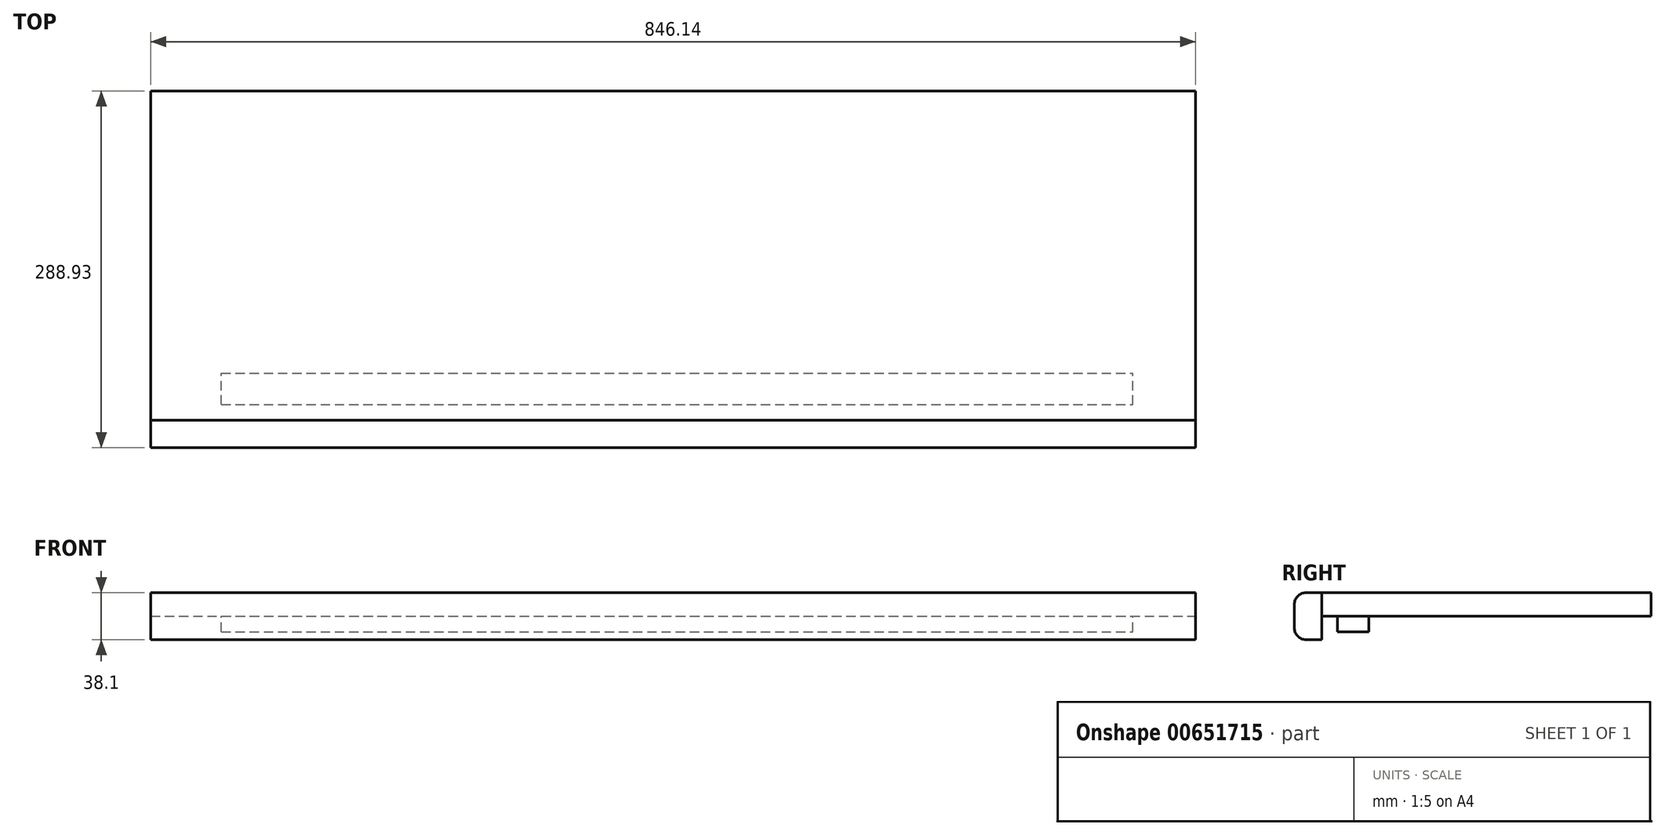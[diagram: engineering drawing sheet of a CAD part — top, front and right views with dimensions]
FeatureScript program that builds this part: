
annotation { "Feature Type Name" : "Feature", "Feature Type Description" : "" }
export const myFeature = defineFeature(function(context is Context, id is Id, definition is map)
    precondition{}
    {
        {
            var Q0;
            Q0=qCreatedBy(makeId("Top.planeOp"),FACE);
            var sketch = newSketch(context, id + "F0", { "sketchPlane" : qUnion([Q0])});
            skLineSegment(sketch, "E0.bottom", {"start": v(0, 0) * mm, "end": v(846.14, 0) * mm});
            skLineSegment(sketch, "E0.top", {"start": v(0, 266.7) * mm, "end": v(846.14, 266.7) * mm});
            skLineSegment(sketch, "E0.left", {"start": v(0, 0) * mm, "end": v(0, 266.7) * mm});
            skLineSegment(sketch, "E0.right", {"start": v(846.14, 0) * mm, "end": v(846.14, 266.7) * mm});
            skSolve(sketch);
        }
        {
            var Q0;
            Q0=makeQuery(id+"F0.imprint","IMPRINT",FACE,{"disambiguationData":[TD([[makeQuery(id+"F0.imprint","IMPRINT",EDGE,{"derivedFrom":sQuery(id+"F0.wireOp",EDGE,"E0.bottom")}),1.0]])]});
            extrude(context, id + "F1", {"entities" : qUnion([Q0]), "depth" : 19.05 * mm, "offsetDistance" : 25.4 * mm});
        }
        {
            var Q0;
            Q0=makeQuery(id+"F1.opExtrude","SWEPT_FACE",FACE,{"disambiguationData":[OSD([sQuery(id+"F0.wireOp",EDGE,"E0.bottom")])]});
            var sketch = newSketch(context, id + "F2", { "sketchPlane" : qUnion([Q0])});
            skLineSegment(sketch, "E1.bottom", {"start": v(0, 19.05) * mm, "end": v(846.14, 19.05) * mm});
            skLineSegment(sketch, "E1.top", {"start": v(0, -19.05) * mm, "end": v(846.14, -19.05) * mm});
            skLineSegment(sketch, "E1.left", {"start": v(0, 19.05) * mm, "end": v(0, -19.05) * mm});
            skLineSegment(sketch, "E1.right", {"start": v(846.14, 19.05) * mm, "end": v(846.14, -19.05) * mm});
            skSolve(sketch);
        }
        {
            var Q0;
            {var subQ0=sQuery(id+"F2.wireOp",EDGE,"E1.top");Q0=makeQuery(id+"F2.imprint","IMPRINT",FACE,{"disambiguationData":[TD([[makeQuery(id+"F2.imprint","IMPRINT",EDGE,{"derivedFrom":subQ0}),1.0]])]});}
            var Q1;
            {var subQ0=sQuery(id+"F2.wireOp",EDGE,"E1.bottom");Q1=makeQuery(id+"F2.imprint","IMPRINT",FACE,{"disambiguationData":[TD([[makeQuery(id+"F2.imprint","IMPRINT",EDGE,{"derivedFrom":subQ0}),-1.0]])]});}
            extrude(context, id + "F3", {"entities" : qUnion([Q0, Q1]), "depth" : 22.22 * mm, "offsetDistance" : 25.4 * mm});
        }
        {
            var Q0;
            Q0=makeQuery(id+"F3.opExtrude","CAP_EDGE",EDGE,{"disambiguationData":[OSD([sQuery(id+"F2.wireOp",EDGE,"E1.bottom")])],"isStart":false});
            var Q1;
            Q1=makeQuery(id+"F3.opExtrude","CAP_EDGE",EDGE,{"disambiguationData":[OSD([sQuery(id+"F2.wireOp",EDGE,"E1.top")])],"isStart":false});
            fillet(context, id + "F4", {"entities" : qUnion([Q0, Q1]), "radius" : 9.52 * mm, "tangentPropagation" : true, "allowEdgeOverflow" : false});
        }
        {
            var Q0;
            Q0=makeQuery(id+"F1.opExtrude","CAP_FACE",FACE,{"disambiguationData":[OSD([sQuery(id+"F0.wireOp",EDGE,"E0.bottom"),sQuery(id+"F0.wireOp",EDGE,"E0.top"),sQuery(id+"F0.wireOp",EDGE,"E0.left"),sQuery(id+"F0.wireOp",EDGE,"E0.right")])],"isStart":true});
            var sketch = newSketch(context, id + "F5", { "sketchPlane" : qUnion([Q0])});
            skLineSegment(sketch, "E2.bottom", {"start": v(57.15, -12.7) * mm, "end": v(795.34, -12.7) * mm});
            skLineSegment(sketch, "E2.top", {"start": v(57.15, -38.1) * mm, "end": v(795.34, -38.1) * mm});
            skLineSegment(sketch, "E2.left", {"start": v(57.15, -12.7) * mm, "end": v(57.15, -38.1) * mm});
            skLineSegment(sketch, "E2.right", {"start": v(795.34, -12.7) * mm, "end": v(795.34, -38.1) * mm});
            skSolve(sketch);
        }
        {
            var Q0;
            Q0=makeQuery(id+"F5.imprint","IMPRINT",FACE,{"disambiguationData":[TD([[makeQuery(id+"F5.imprint","IMPRINT",EDGE,{"derivedFrom":sQuery(id+"F5.wireOp",EDGE,"E2.bottom")}),-1.0]])]});
            extrude(context, id + "F6", {"entities" : qUnion([Q0]), "depth" : 12.7 * mm, "offsetDistance" : 25.4 * mm});
        }
    });
